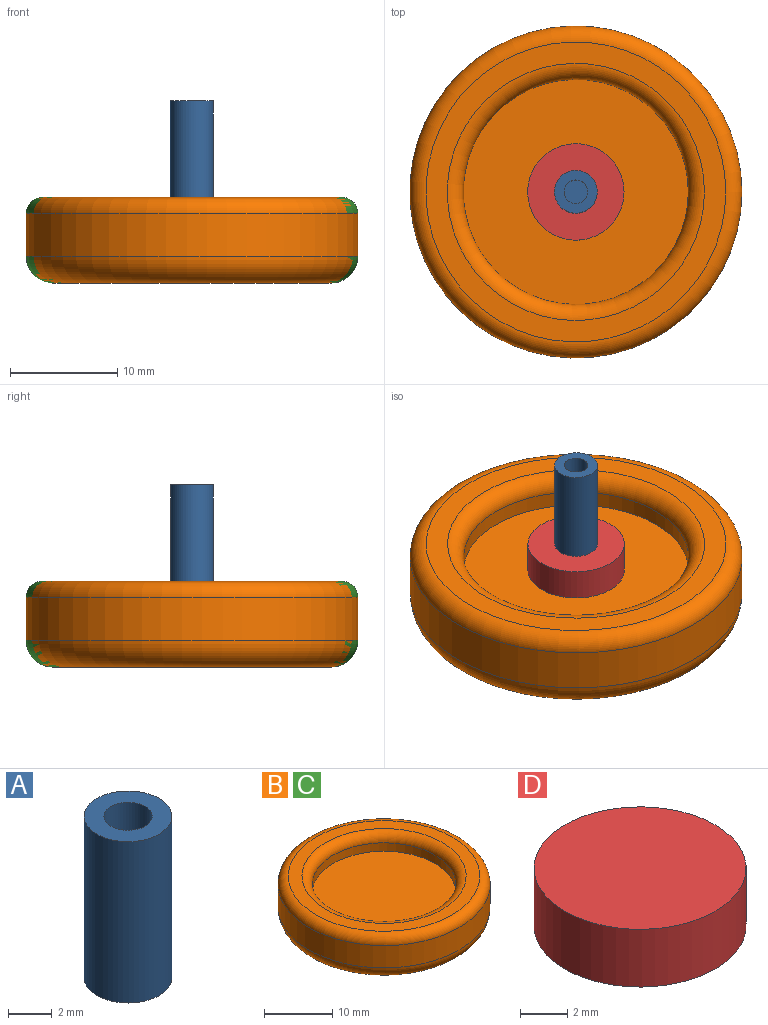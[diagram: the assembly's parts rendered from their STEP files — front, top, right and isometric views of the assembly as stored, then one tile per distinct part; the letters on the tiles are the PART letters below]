
ASSEMBLY  parts=4 mates=2
PART A: 5 faces, bbox 4x4x9 mm
  f0: cylinder r=2mm len=9mm, axis (0,0,-1), area 113.1mm2, adj f1,f2
  f1: plane 4x4mm, normal (0,0,1), area 8.8mm2, adj f0,f3
  f2: plane 4x4mm, normal (0,0,-1), area 12.6mm2, adj f0
  f3: cylinder r=1.1mm len=8.1mm, axis (0,0,-1), area 56mm2, adj f1,f4
  f4: plane 2.2x2.2mm, normal (0,0,1), area 3.8mm2, adj f3
PART B: 8 faces, bbox 33.6x33.6x8 mm
  f0: cylinder r=15.5mm len=31mm, axis (0,0,-1), area 389.6mm2, adj f6,f7
  f1: plane 28x28mm, normal (0,0,1), area 163.4mm2, adj f5,f6
  f2: plane 26x26mm, normal (0,0,-1), area 530.9mm2, adj f7
  f3: cylinder r=10.5mm len=21mm, axis (0,0,-1), area 99mm2, adj f4,f5
  f4: plane 21x21mm, normal (0,0,1), area 346.4mm2, adj f3
  f5: torus R=12mm, axis (0,0,1), area 163.5mm2, adj f1,f3
  f6: torus R=14mm, axis (0,0,1), area 221.4mm2, adj f0,f1
  f7: torus R=13mm, axis (0,0,1), area 360mm2, adj f0,f2
PART C: same geometry as B
PART D: 3 faces, bbox 9x9x3 mm
  f0: cylinder r=4.5mm len=9mm, axis (0,0,-1), area 84.8mm2, adj f1,f2
  f1: plane 9x9mm, normal (0,0,1), area 63.6mm2, adj f0
  f2: plane 9x9mm, normal (0,0,-1), area 63.6mm2, adj f0
PLACE A t=(-11.16,-11.48,8.93)mm
PLACE B t=(-5.87,-7.81,0.93)mm fixed
PLACE C t=(-5.87,-7.81,0.93)mm
PLACE D t=(-16.33,-10.82,5.93)mm
MATE slider D.f0 <-> A.f0  axis (0,0,1) through (-19.22,-7.81,8.93)mm
MATE slider B.f0 <-> D.f0  axis (0,0,1) through (-19.22,-7.81,5.93)mm
